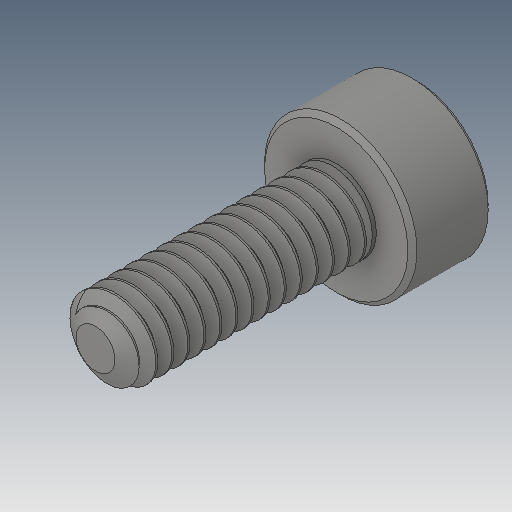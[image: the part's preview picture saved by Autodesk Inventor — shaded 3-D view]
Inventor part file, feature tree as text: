
AUTODESK INVENTOR PART (.ipt)
format: ipt  version: 2019 (Build 230136000, 136)  size: 638,976 bytes
history: native  units: in
note: dims shown in document units (in); Inventor stores cm internally (conversion verified against a paired STEP export)
features: revolve x1
ambient origin geometry x8: Origin, YZ Plane, XZ Plane, XY Plane, X Axis, Y Axis, Z Axis, Center Point
bodies: Solid1 (feature_tree)
feature tree (1):
  revolve  "Revolve1"  [1 undecoded]
note: 1 required parameter value undecoded (feature->parameter linkage not recoverable at this tier; creation-order binding heuristic only, values carry confidence <= 0.55)
